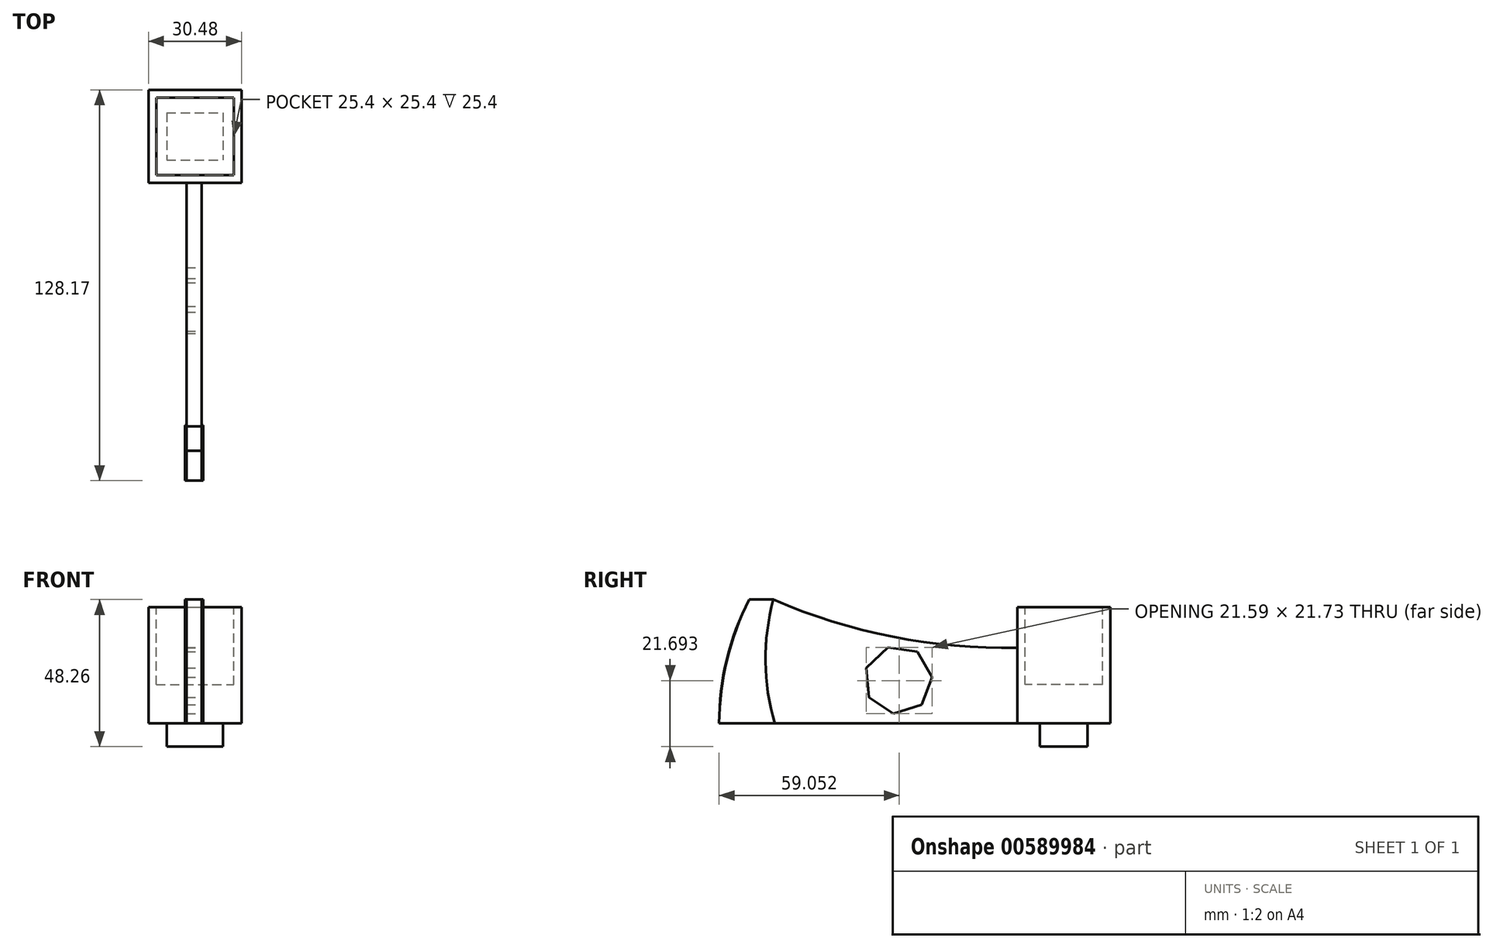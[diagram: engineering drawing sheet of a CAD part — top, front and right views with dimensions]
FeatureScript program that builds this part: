
annotation { "Feature Type Name" : "Feature", "Feature Type Description" : "" }
export const myFeature = defineFeature(function(context is Context, id is Id, definition is map)
    precondition{}
    {
        {
            var Q0;
            Q0=qCreatedBy(makeId("Top.planeOp"),FACE);
            var sketch = newSketch(context, id + "F0", { "sketchPlane" : qUnion([Q0])});
            skPoint(sketch, "E0.0", {"position": v(0, 0) * mm});
            skLineSegment(sketch, "E1.bottom", {"start": v(0, 0) * mm, "end": v(30.48, 0) * mm});
            skLineSegment(sketch, "E1.top", {"start": v(0, 30.48) * mm, "end": v(30.48, 30.48) * mm});
            skLineSegment(sketch, "E1.left", {"start": v(0, 0) * mm, "end": v(0, 30.48) * mm});
            skLineSegment(sketch, "E1.right", {"start": v(30.48, 0) * mm, "end": v(30.48, 30.48) * mm});
            skSolve(sketch);
        }
        {
            var Q0;
            Q0=makeQuery(id+"F0.imprint","IMPRINT",FACE,{"disambiguationData":[TD([[makeQuery(id+"F0.imprint","IMPRINT",EDGE,{"derivedFrom":sQuery(id+"F0.wireOp",EDGE,"E1.bottom")}),1.0]])]});
            extrude(context, id + "F1", {"entities" : qUnion([Q0]), "endBound" : BoundingType.SYMMETRIC, "oppositeDirection" : true, "depth" : 38.1 * mm, "offsetDistance" : 25.4 * mm});
        }
        {
            var Q0;
            Q0=makeQuery(id+"F1.opExtrude","CAP_FACE",FACE,{"disambiguationData":[OSD([sQuery(id+"F0.wireOp",EDGE,"E1.bottom"),sQuery(id+"F0.wireOp",EDGE,"E1.top"),sQuery(id+"F0.wireOp",EDGE,"E1.left"),sQuery(id+"F0.wireOp",EDGE,"E1.right")])],"isStart":false});
            var sketch = newSketch(context, id + "F2", { "sketchPlane" : qUnion([Q0])});
            skLineSegment(sketch, "E2.bottom", {"start": v(5.98, -23) * mm, "end": v(24.5, -23) * mm});
            skLineSegment(sketch, "E2.top", {"start": v(5.98, -7.48) * mm, "end": v(24.5, -7.48) * mm});
            skLineSegment(sketch, "E2.left", {"start": v(5.98, -23) * mm, "end": v(5.98, -7.48) * mm});
            skLineSegment(sketch, "E2.right", {"start": v(24.5, -23) * mm, "end": v(24.5, -7.48) * mm});
            skPoint(sketch, "E2.middle", {"position": v(15.24, -15.24) * mm});
            skPoint(sketch, "E2.middle.positionSnap0", {"position": v(15.24, 0) * mm});
            skPoint(sketch, "E2.middle.positionSnap1", {"position": v(0, -15.24) * mm});
            skPoint(sketch, "E2.centerSnap0", {"position": v(15.24, 0) * mm});
            skPoint(sketch, "E2.centerSnap1", {"position": v(0, -15.24) * mm});
            skSolve(sketch);
        }
        {
            var Q0;
            Q0=makeQuery(id+"F2.imprint","IMPRINT",FACE,{"disambiguationData":[TD([[makeQuery(id+"F2.imprint","IMPRINT",EDGE,{"derivedFrom":sQuery(id+"F2.wireOp",EDGE,"E2.bottom")}),1.0]])]});
            extrude(context, id + "F3", {"entities" : qUnion([Q0]), "operationType" : NewBodyOperationType.ADD, "depth" : 7.62 * mm, "offsetDistance" : 25.4 * mm});
        }
        {
            var Q0;
            Q0=qCreatedBy(makeId("Top.planeOp"),FACE);
            var sketch = newSketch(context, id + "F4", { "sketchPlane" : qUnion([Q0])});
            skLineSegment(sketch, "E3.0", {"start": v(0, 0) * mm, "end": v(30.48, 0) * mm});
            skLineSegment(sketch, "E4", {"start": v(14.97, -97.69) * mm, "end": v(12.43, -97.69) * mm});
            skLineSegment(sketch, "E5", {"start": v(12.43, -97.69) * mm, "end": v(12.43, 0) * mm});
            skLineSegment(sketch, "E6", {"start": v(14.97, -97.69) * mm, "end": v(17.5, -97.69) * mm});
            skLineSegment(sketch, "E7", {"start": v(17.5, -97.69) * mm, "end": v(17.5, 0) * mm});
            skSolve(sketch);
        }
        {
            var Q0;
            Q0 = qSketchRegion(id + "F4", true);
            extrude(context, id + "F5", {"entities" : qUnion([Q0]), "operationType" : NewBodyOperationType.ADD, "endBound" : BoundingType.SYMMETRIC, "depth" : 43.18 * mm, "offsetDistance" : 25.4 * mm});
        }
        {
            var Q0;
            Q0=makeQuery(id+"F5.opExtrude","SWEPT_FACE",FACE,{"disambiguationData":[OSD([sQuery(id+"F4.wireOp",EDGE,"E7")])]});
            var sketch = newSketch(context, id + "F6", { "sketchPlane" : qUnion([Q0])});
            skLineSegment(sketch, "E8.0", {"start": v(0, -19.05) * mm, "end": v(0, 19.05) * mm});
            skLineSegment(sketch, "E9", {"start": v(0, -19.05) * mm, "end": v(-97.69, -19.05) * mm});
            skLineSegment(sketch, "E10", {"start": v(-97.69, -19.05) * mm, "end": v(-97.69, -21.59) * mm});
            skLineSegment(sketch, "E11", {"start": v(-97.69, -21.59) * mm, "end": v(0, -21.59) * mm});
            skLineSegment(sketch, "E12", {"start": v(0, -21.59) * mm, "end": v(0, -19.05) * mm});
            skLineSegment(sketch, "E13", {"start": v(-67.4, 21.59) * mm, "end": v(0, 21.59) * mm});
            skLineSegment(sketch, "E14", {"start": v(0, 21.59) * mm, "end": v(0, 9.35) * mm});
            skLineSegment(sketch, "E15", {"start": v(-97.69, -21.59) * mm, "end": v(-97.69, -21.59) * mm});
            skLineSegment(sketch, "E16", {"start": v(-97.69, -21.59) * mm, "end": v(-97.69, -19.05) * mm});
            skArc(sketch, "E17", {"start": v(-79.92, 21.59) * mm, "mid": v(-40.8, 9.4) * mm, "end": v(0, 5.77) * mm});
            skLineSegment(sketch, "E18", {"start": v(0, 5.77) * mm, "end": v(0, 9.35) * mm});
            skLineSegment(sketch, "E19", {"start": v(-67.4, 21.59) * mm, "end": v(-79.92, 21.59) * mm});
            skSolve(sketch);
        }
        {
            var Q0;
            Q0 = qSketchRegion(id + "F6", true);
            extrude(context, id + "F7", {"entities" : qUnion([Q0]), "operationType" : NewBodyOperationType.REMOVE, "oppositeDirection" : true, "depth" : 25.4 * mm, "offsetDistance" : 25.4 * mm});
        }
        {
            var Q0;
            Q0=makeQuery(id+"F5.opExtrude","SWEPT_FACE",FACE,{"disambiguationData":[OSD([sQuery(id+"F4.wireOp",EDGE,"E7")])]});
            var sketch = newSketch(context, id + "F8", { "sketchPlane" : qUnion([Q0])});
            skArc(sketch, "E20", {"start": v(-87.83, 21.6) * mm, "mid": v(-95.19, 1.86) * mm, "end": v(-97.69, -19.05) * mm});
            skLineSegment(sketch, "E21", {"start": v(-97.69, -19.05) * mm, "end": v(-97.69, 21.59) * mm});
            skLineSegment(sketch, "E22", {"start": v(-97.69, 21.59) * mm, "end": v(-87.83, 21.6) * mm});
            skSolve(sketch);
        }
        {
            var Q0;
            Q0 = qSketchRegion(id + "F8", true);
            extrude(context, id + "F9", {"entities" : qUnion([Q0]), "operationType" : NewBodyOperationType.REMOVE, "oppositeDirection" : true, "depth" : 25.4 * mm, "offsetDistance" : 25.4 * mm});
        }
        {
            var Q0;
            Q0=makeQuery(id+"F5.opExtrude","SWEPT_FACE",FACE,{"disambiguationData":[OSD([sQuery(id+"F4.wireOp",EDGE,"E7")])]});
            var sketch = newSketch(context, id + "F10", { "sketchPlane" : qUnion([Q0])});
            skArc(sketch, "E23", {"start": v(-79.92, 21.59) * mm, "mid": v(-82.5, 1.24) * mm, "end": v(-79.45, -19.05) * mm});
            skLineSegment(sketch, "E24", {"start": v(-79.92, 21.59) * mm, "end": v(-87.83, 21.6) * mm});
            skArc(sketch, "E25", {"start": v(-87.83, 21.6) * mm, "mid": v(-95.12, 1.84) * mm, "end": v(-97.69, -19.05) * mm});
            skLineSegment(sketch, "E26", {"start": v(-97.69, -19.05) * mm, "end": v(-79.45, -19.05) * mm});
            skSolve(sketch);
        }
        {
            var Q0;
            Q0 = qSketchRegion(id + "F10", true);
            extrude(context, id + "F11", {"entities" : qUnion([Q0]), "depth" : 0.5 * mm, "offsetDistance" : 25.4 * mm});
        }
        {
            var Q0;
            Q0=makeQuery(id+"F5.opExtrude","SWEPT_FACE",FACE,{"disambiguationData":[OSD([sQuery(id+"F4.wireOp",EDGE,"E5")])]});
            var sketch = newSketch(context, id + "F12", { "sketchPlane" : qUnion([Q0])});
            skArc(sketch, "E27.0", {"start": v(79.92, 21.59) * mm, "mid": v(82.5, 1.24) * mm, "end": v(79.45, -19.05) * mm});
            skLineSegment(sketch, "E28.0", {"start": v(79.45, -19.05) * mm, "end": v(97.69, -19.05) * mm});
            skArc(sketch, "E29.0", {"start": v(87.83, 21.59) * mm, "mid": v(95.12, 1.84) * mm, "end": v(97.69, -19.05) * mm});
            skLineSegment(sketch, "E30.0", {"start": v(87.83, 21.59) * mm, "end": v(79.92, 21.59) * mm});
            skLineSegment(sketch, "E31", {"start": v(79.92, 21.59) * mm, "end": v(87.83, 21.6) * mm});
            skArc(sketch, "E32", {"start": v(79.45, -19.05) * mm, "mid": v(82.34, 1.24) * mm, "end": v(79.92, 21.59) * mm});
            skArc(sketch, "E33", {"start": v(97.69, -19.05) * mm, "mid": v(95.11, 1.84) * mm, "end": v(87.83, 21.59) * mm});
            skSolve(sketch);
        }
        {
            var Q0;
            Q0 = qSketchRegion(id + "F12", true);
            extrude(context, id + "F13", {"entities" : qUnion([Q0]), "depth" : 0.5 * mm, "offsetDistance" : 25.4 * mm});
        }
        {
            var Q0;
            Q0=makeQuery(id+"F11.opExtrude","CAP_FACE",FACE,{"disambiguationData":[OSD([sQuery(id+"F10.wireOp",EDGE,"E23"),sQuery(id+"F10.wireOp",EDGE,"E24"),sQuery(id+"F10.wireOp",EDGE,"E25"),sQuery(id+"F10.wireOp",EDGE,"E26")])],"isStart":false});
            var sketch = newSketch(context, id + "F14", { "sketchPlane" : qUnion([Q0])});
            skCircle(sketch, "E34.cCircle", {"center": v(-38.99, -4.77) * mm, "radius": 10.07 * mm, "construction": true});
            skLineSegment(sketch, "E34.0", {"start": v(-27.84, -3.83) * mm, "end": v(-31.3, -12.9) * mm});
            skLineSegment(sketch, "E34.1", {"start": v(-31.3, -12.9) * mm, "end": v(-40.55, -15.84) * mm});
            skLineSegment(sketch, "E34.2", {"start": v(-40.55, -15.84) * mm, "end": v(-48.62, -10.45) * mm});
            skLineSegment(sketch, "E34.3", {"start": v(-48.62, -10.45) * mm, "end": v(-49.43, -0.78) * mm});
            skLineSegment(sketch, "E34.4", {"start": v(-49.43, -0.78) * mm, "end": v(-42.38, 5.89) * mm});
            skLineSegment(sketch, "E34.5", {"start": v(-42.38, 5.89) * mm, "end": v(-32.77, 4.53) * mm});
            skLineSegment(sketch, "E34.6", {"start": v(-32.77, 4.53) * mm, "end": v(-27.84, -3.83) * mm});
            skPoint(sketch, "E34.0.midPoint", {"position": v(-29.58, -8.36) * mm});
            skSolve(sketch);
        }
        {
            var Q0;
            Q0 = qSketchRegion(id + "F14", true);
            extrude(context, id + "F15", {"entities" : qUnion([Q0]), "operationType" : NewBodyOperationType.REMOVE, "oppositeDirection" : true, "depth" : 25.4 * mm, "offsetDistance" : 25.4 * mm});
        }
        {
            var Q0;
            Q0=makeQuery(id+"F1.opExtrude","CAP_FACE",FACE,{"disambiguationData":[OSD([sQuery(id+"F0.wireOp",EDGE,"E1.bottom"),sQuery(id+"F0.wireOp",EDGE,"E1.top"),sQuery(id+"F0.wireOp",EDGE,"E1.left"),sQuery(id+"F0.wireOp",EDGE,"E1.right")])],"isStart":true});
            var sketch = newSketch(context, id + "F16", { "sketchPlane" : qUnion([Q0])});
            skLineSegment(sketch, "E35.bottom", {"start": v(2.54, 27.94) * mm, "end": v(27.94, 27.94) * mm});
            skLineSegment(sketch, "E35.top", {"start": v(2.54, 2.54) * mm, "end": v(27.94, 2.54) * mm});
            skLineSegment(sketch, "E35.left", {"start": v(2.54, 27.94) * mm, "end": v(2.54, 2.54) * mm});
            skLineSegment(sketch, "E35.right", {"start": v(27.94, 27.94) * mm, "end": v(27.94, 2.54) * mm});
            skPoint(sketch, "E35.middle", {"position": v(15.24, 15.24) * mm});
            skPoint(sketch, "E35.middle.positionSnap0", {"position": v(15.24, 0) * mm});
            skPoint(sketch, "E35.middle.positionSnap1", {"position": v(0, 15.24) * mm});
            skPoint(sketch, "E35.centerSnap0", {"position": v(15.24, 0) * mm});
            skPoint(sketch, "E35.centerSnap1", {"position": v(0, 15.24) * mm});
            skSolve(sketch);
        }
        {
            var Q0;
            Q0 = qSketchRegion(id + "F16", true);
            extrude(context, id + "F17", {"entities" : qUnion([Q0]), "operationType" : NewBodyOperationType.REMOVE, "oppositeDirection" : true, "depth" : 25.4 * mm, "offsetDistance" : 25.4 * mm});
        }
    });
